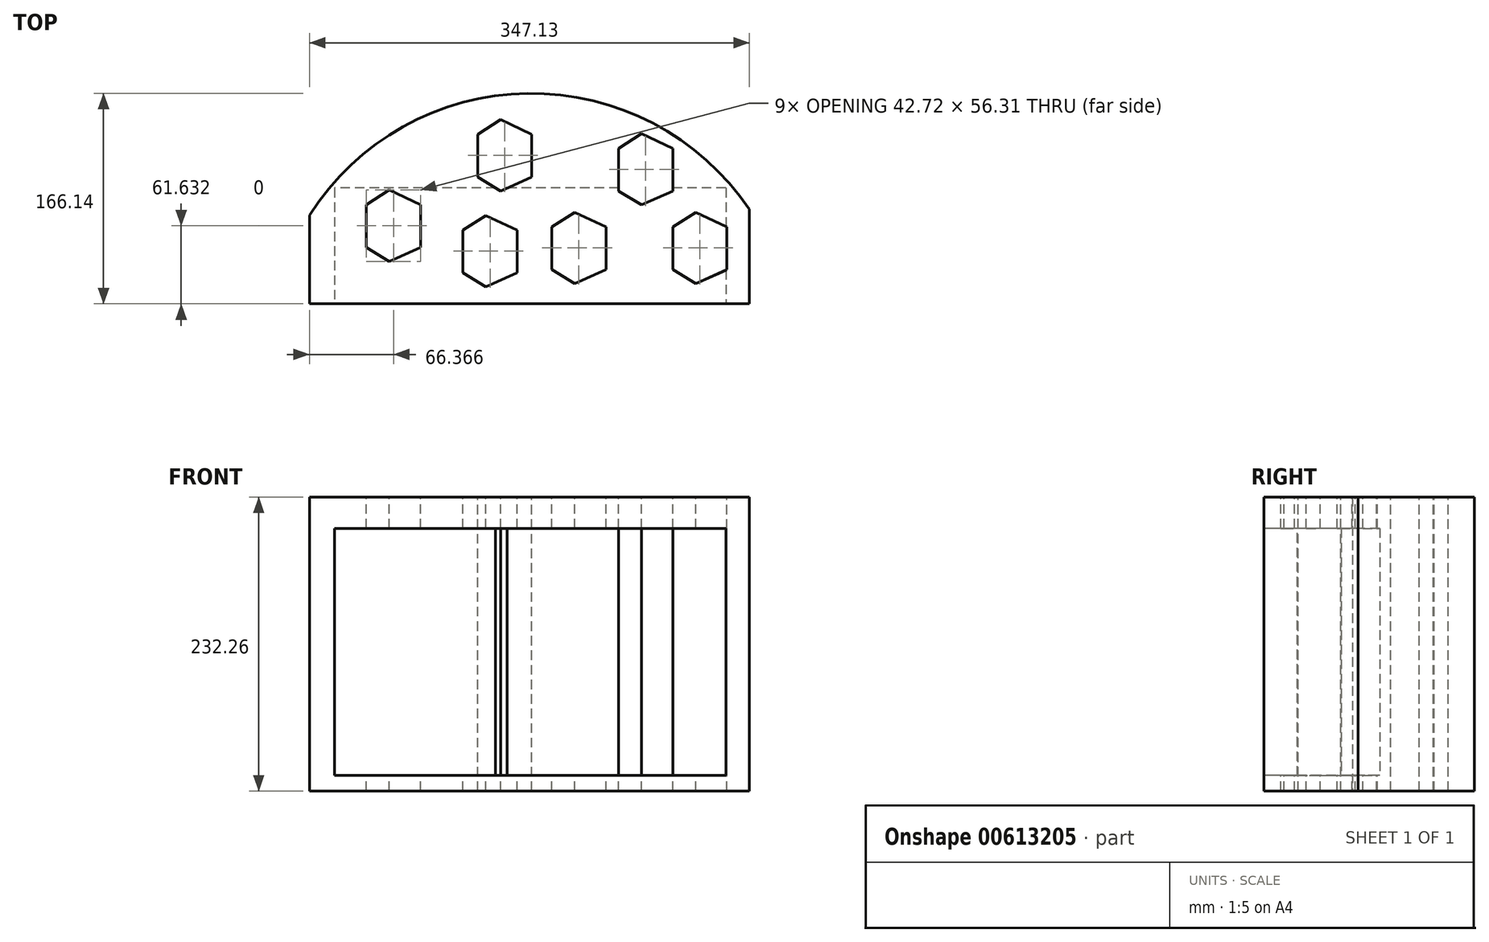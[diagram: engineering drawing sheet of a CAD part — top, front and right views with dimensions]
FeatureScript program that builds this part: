
annotation { "Feature Type Name" : "Feature", "Feature Type Description" : "" }
export const myFeature = defineFeature(function(context is Context, id is Id, definition is map)
    precondition{}
    {
        {
            var Q0;
            Q0=qCreatedBy(makeId("Top.planeOp"),FACE);
            var sketch = newSketch(context, id + "F0", { "sketchPlane" : qUnion([Q0])});
            skLineSegment(sketch, "E0.0", {"start": v(173.77, 23.1) * mm, "end": v(173.77, -51.43) * mm});
            skLineSegment(sketch, "E1.0", {"start": v(-173.36, -51.43) * mm, "end": v(173.77, -51.43) * mm});
            skArc(sketch, "E2.0", {"start": v(-173.36, 18.4) * mm, "mid": v(-1.06, 114.7) * mm, "end": v(173.77, 23.1) * mm});
            skLineSegment(sketch, "E3.0", {"start": v(-173.36, 18.4) * mm, "end": v(-173.36, -51.43) * mm});
            skLineSegment(sketch, "E4", {"start": v(-173.36, -51.43) * mm, "end": v(-173.36, 18.4) * mm});
            skLineSegment(sketch, "E5", {"start": v(173.77, -51.43) * mm, "end": v(173.77, 23.1) * mm});
            skArc(sketch, "E6", {"start": v(173.77, 23.1) * mm, "mid": v(-1.06, 114.04) * mm, "end": v(-173.36, 18.4) * mm});
            skSolve(sketch);
        }
        {
            var Q0;
            Q0 = qSketchRegion(id + "F0", true);
            extrude(context, id + "F1", {"entities" : qUnion([Q0]), "depth" : 232.26 * mm, "offsetDistance" : 25.4 * mm});
        }
        {
            var Q0;
            Q0=makeQuery(id+"F1.opExtrude","SWEPT_FACE",FACE,{"disambiguationData":[OSD([sQuery(id+"F0.wireOp",EDGE,"E1.0")])]});
            var sketch = newSketch(context, id + "F2", { "sketchPlane" : qUnion([Q0])});
            skLineSegment(sketch, "E7", {"start": v(155.25, 12.26) * mm, "end": v(-153.67, 12.26) * mm});
            skLineSegment(sketch, "E8", {"start": v(-153.67, 12.26) * mm, "end": v(-153.67, 207.5) * mm});
            skLineSegment(sketch, "E9", {"start": v(-153.67, 207.5) * mm, "end": v(155.25, 207.5) * mm});
            skLineSegment(sketch, "E10", {"start": v(155.25, 207.5) * mm, "end": v(155.25, 12.26) * mm});
            skSolve(sketch);
        }
        {
            var Q0;
            Q0 = qSketchRegion(id + "F2", true);
            extrude(context, id + "F3", {"entities" : qUnion([Q0]), "operationType" : NewBodyOperationType.REMOVE, "oppositeDirection" : true, "depth" : 91.44 * mm, "offsetDistance" : 25.4 * mm});
        }
        {
            var Q0;
            Q0=makeQuery(id+"F1.opExtrude","CAP_FACE",FACE,{"disambiguationData":[OSD([sQuery(id+"F0.wireOp",EDGE,"E2.0"),sQuery(id+"F0.wireOp",EDGE,"E4"),sQuery(id+"F0.wireOp",EDGE,"E1.0"),sQuery(id+"F0.wireOp",EDGE,"E5")])],"isStart":false});
            var sketch = newSketch(context, id + "F4", { "sketchPlane" : qUnion([Q0])});
            skLineSegment(sketch, "E11", {"start": v(-128.35, -6.95) * mm, "end": v(-128.35, 26.7) * mm});
            skLineSegment(sketch, "E12", {"start": v(-128.35, -6.95) * mm, "end": v(-110.23, -17.95) * mm});
            skLineSegment(sketch, "E13", {"start": v(-110.23, -17.95) * mm, "end": v(-85.64, -6.95) * mm});
            skLineSegment(sketch, "E14", {"start": v(-85.64, 26.7) * mm, "end": v(-85.64, -6.95) * mm});
            skLineSegment(sketch, "E15", {"start": v(-85.64, 26.7) * mm, "end": v(-110.23, 38.36) * mm});
            skLineSegment(sketch, "E16", {"start": v(-110.23, 38.36) * mm, "end": v(-128.35, 26.7) * mm});
            skLineSegment(sketch, "E17", {"start": v(-40.65, 48.65) * mm, "end": v(-40.65, 82.3) * mm});
            skLineSegment(sketch, "E18", {"start": v(-40.65, 48.65) * mm, "end": v(-22.53, 37.65) * mm});
            skLineSegment(sketch, "E19", {"start": v(-22.53, 37.65) * mm, "end": v(2.07, 48.65) * mm});
            skLineSegment(sketch, "E20", {"start": v(2.07, 82.3) * mm, "end": v(2.07, 48.65) * mm});
            skLineSegment(sketch, "E21", {"start": v(2.07, 82.3) * mm, "end": v(-22.53, 93.96) * mm});
            skLineSegment(sketch, "E22", {"start": v(-22.53, 93.96) * mm, "end": v(-40.65, 82.3) * mm});
            skLineSegment(sketch, "E23", {"start": v(70.68, 37.65) * mm, "end": v(70.68, 71.3) * mm});
            skLineSegment(sketch, "E24", {"start": v(70.68, 37.65) * mm, "end": v(88.8, 26.64) * mm});
            skLineSegment(sketch, "E25", {"start": v(88.8, 26.64) * mm, "end": v(113.4, 37.65) * mm});
            skLineSegment(sketch, "E26", {"start": v(113.4, 71.3) * mm, "end": v(113.4, 37.65) * mm});
            skLineSegment(sketch, "E27", {"start": v(113.4, 71.3) * mm, "end": v(88.8, 82.95) * mm});
            skLineSegment(sketch, "E28", {"start": v(88.8, 82.95) * mm, "end": v(70.68, 71.3) * mm});
            skLineSegment(sketch, "E29", {"start": v(17.95, -24.48) * mm, "end": v(17.95, 9.17) * mm});
            skLineSegment(sketch, "E30", {"start": v(17.95, -24.48) * mm, "end": v(36.08, -35.48) * mm});
            skLineSegment(sketch, "E31", {"start": v(36.08, -35.48) * mm, "end": v(60.67, -24.48) * mm});
            skLineSegment(sketch, "E32", {"start": v(60.67, 9.17) * mm, "end": v(60.67, -24.48) * mm});
            skLineSegment(sketch, "E33", {"start": v(60.67, 9.17) * mm, "end": v(36.08, 20.82) * mm});
            skLineSegment(sketch, "E34", {"start": v(36.08, 20.82) * mm, "end": v(17.95, 9.17) * mm});
            skLineSegment(sketch, "E35", {"start": v(-52.13, -27.04) * mm, "end": v(-52.13, 6.62) * mm});
            skLineSegment(sketch, "E36", {"start": v(-52.13, -27.04) * mm, "end": v(-34, -38.04) * mm});
            skLineSegment(sketch, "E37", {"start": v(-34, -38.04) * mm, "end": v(-9.41, -27.04) * mm});
            skLineSegment(sketch, "E38", {"start": v(-9.41, 6.62) * mm, "end": v(-9.41, -27.04) * mm});
            skLineSegment(sketch, "E39", {"start": v(-9.41, 6.62) * mm, "end": v(-34, 18.27) * mm});
            skLineSegment(sketch, "E40", {"start": v(-34, 18.27) * mm, "end": v(-52.13, 6.62) * mm});
            skLineSegment(sketch, "E41", {"start": v(113.4, -24.48) * mm, "end": v(113.4, 9.17) * mm});
            skLineSegment(sketch, "E42", {"start": v(113.4, -24.48) * mm, "end": v(131.52, -35.48) * mm});
            skLineSegment(sketch, "E43", {"start": v(131.52, -35.48) * mm, "end": v(156.12, -24.48) * mm});
            skLineSegment(sketch, "E44", {"start": v(156.12, 9.17) * mm, "end": v(156.12, -24.48) * mm});
            skLineSegment(sketch, "E45", {"start": v(156.12, 9.17) * mm, "end": v(131.52, 20.82) * mm});
            skLineSegment(sketch, "E46", {"start": v(131.52, 20.82) * mm, "end": v(113.4, 9.17) * mm});
            skSolve(sketch);
        }
        {
            var Q0;
            Q0=makeQuery(id+"F4.imprint","IMPRINT",FACE,{"disambiguationData":[TD([[makeQuery(id+"F4.imprint","IMPRINT",EDGE,{"derivedFrom":sQuery(id+"F4.wireOp",EDGE,"E11")}),-1.0]])]});
            var Q1;
            Q1=makeQuery(id+"F4.imprint","IMPRINT",FACE,{"disambiguationData":[TD([[makeQuery(id+"F4.imprint","IMPRINT",EDGE,{"derivedFrom":sQuery(id+"F4.wireOp",EDGE,"E35")}),-1.0]])]});
            var Q2;
            Q2=makeQuery(id+"F4.imprint","IMPRINT",FACE,{"disambiguationData":[TD([[makeQuery(id+"F4.imprint","IMPRINT",EDGE,{"derivedFrom":sQuery(id+"F4.wireOp",EDGE,"E29")}),-1.0]])]});
            var Q3;
            Q3=makeQuery(id+"F4.imprint","IMPRINT",FACE,{"disambiguationData":[TD([[makeQuery(id+"F4.imprint","IMPRINT",EDGE,{"derivedFrom":sQuery(id+"F4.wireOp",EDGE,"E41")}),-1.0]])]});
            var Q4;
            Q4=makeQuery(id+"F4.imprint","IMPRINT",FACE,{"disambiguationData":[TD([[makeQuery(id+"F4.imprint","IMPRINT",EDGE,{"derivedFrom":sQuery(id+"F4.wireOp",EDGE,"E23")}),-1.0]])]});
            var Q5;
            Q5=makeQuery(id+"F4.imprint","IMPRINT",FACE,{"disambiguationData":[TD([[makeQuery(id+"F4.imprint","IMPRINT",EDGE,{"derivedFrom":sQuery(id+"F4.wireOp",EDGE,"E17")}),-1.0]])]});
            extrude(context, id + "F5", {"entities" : qUnion([Q0, Q1, Q2, Q3, Q4, Q5]), "operationType" : NewBodyOperationType.REMOVE, "oppositeDirection" : true, "depth" : 508 * mm, "offsetDistance" : 25.4 * mm});
        }
    });
